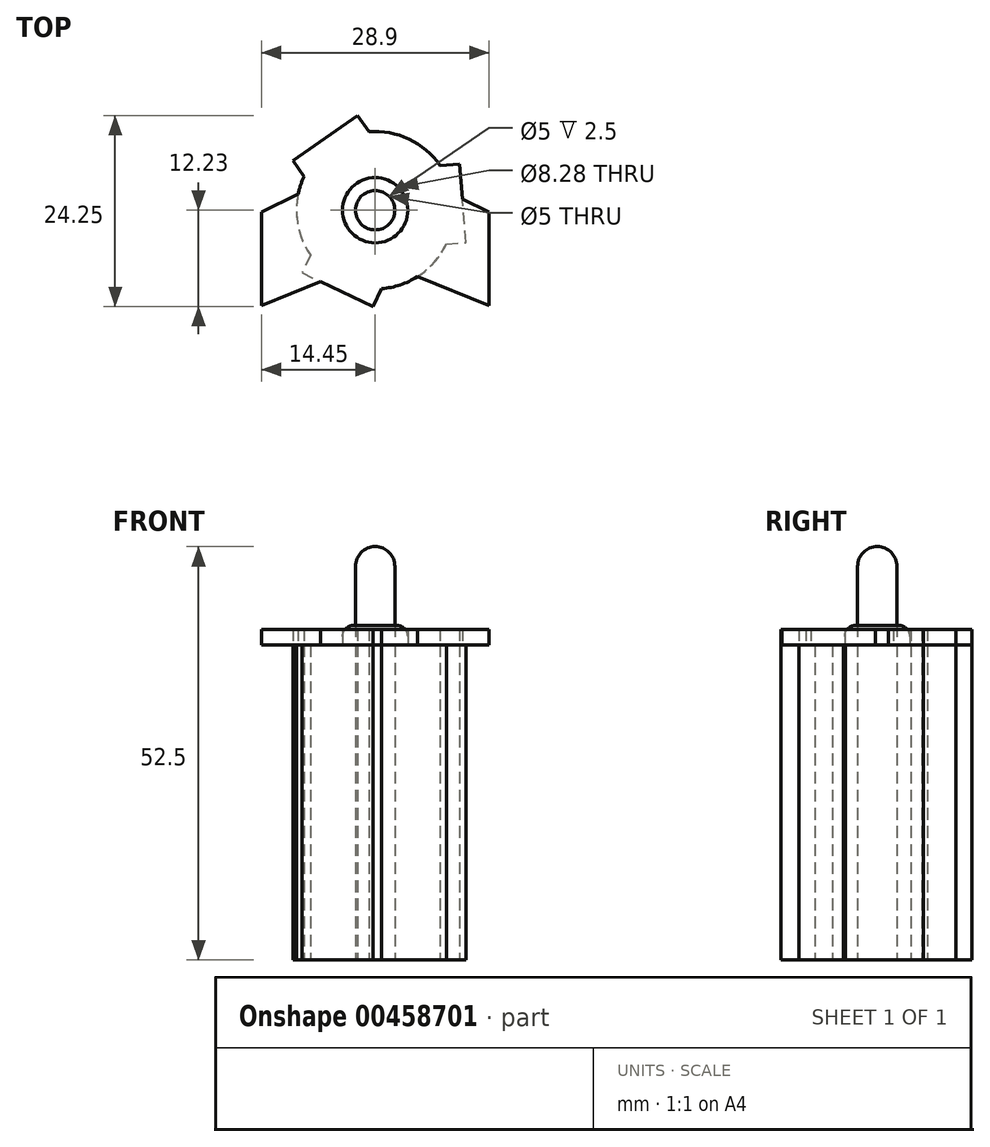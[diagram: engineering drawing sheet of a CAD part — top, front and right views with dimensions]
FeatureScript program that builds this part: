
annotation { "Feature Type Name" : "Feature", "Feature Type Description" : "" }
export const myFeature = defineFeature(function(context is Context, id is Id, definition is map)
    precondition{}
    {
        {
            var Q0;
            Q0=qCreatedBy(makeId("Top.planeOp"),FACE);
            var sketch = newSketch(context, id + "F0", { "sketchPlane" : qUnion([Q0])});
            skCircle(sketch, "E0", {"center": v(0, 0) * mm, "radius": 10 * mm});
            skLineSegment(sketch, "E1", {"start": v(-9.04, 4.28) * mm, "end": v(-0.81, 9.97) * mm});
            skLineSegment(sketch, "E2", {"start": v(-0.81, 9.97) * mm, "end": v(-2.23, 12.02) * mm});
            skLineSegment(sketch, "E3", {"start": v(-2.23, 12.02) * mm, "end": v(-10.46, 6.34) * mm});
            skLineSegment(sketch, "E4", {"start": v(-10.46, 6.34) * mm, "end": v(-9.04, 4.28) * mm});
            skLineSegment(sketch, "E5.1.0", {"start": v(-8.23, -5.69) * mm, "end": v(-9.3, -7.95) * mm});
            skLineSegment(sketch, "E5.1.1", {"start": v(-0.26, -12.23) * mm, "end": v(0.81, -9.97) * mm});
            skLineSegment(sketch, "E5.1.2", {"start": v(-9.3, -7.95) * mm, "end": v(-0.26, -12.23) * mm});
            skLineSegment(sketch, "E5.2.0", {"start": v(9.04, -4.28) * mm, "end": v(11.53, -4.08) * mm});
            skLineSegment(sketch, "E5.2.1", {"start": v(10.72, 5.89) * mm, "end": v(8.23, 5.69) * mm});
            skLineSegment(sketch, "E5.2.2", {"start": v(11.53, -4.08) * mm, "end": v(10.72, 5.89) * mm});
            skCircle(sketch, "E6", {"center": v(0, 0) * mm, "radius": 2.5 * mm});
            skSolve(sketch);
        }
        {
            var Q0;
            Q0 = qSketchRegion(id + "F0", true);
            extrude(context, id + "F1", {"entities" : qUnion([Q0]), "depth" : 40 * mm, "offsetDistance" : 25 * mm});
        }
        {
            var Q0;
            Q0=makeQuery(id+"F0.imprint","IMPRINT",FACE,{"disambiguationData":[TD([[makeQuery(id+"F0.imprint","IMPRINT",EDGE,{"derivedFrom":sQuery(id+"F0.wireOp",EDGE,"E6")}),1.0]])]});
            extrude(context, id + "F2", {"entities" : qUnion([Q0]), "depth" : 40 * mm, "offsetDistance" : 25 * mm});
        }
        {
            var Q0;
            Q0=makeQuery(id+"F1.opExtrude","CAP_FACE",FACE,{"disambiguationData":[OSD([sQuery(id+"F0.wireOp",EDGE,"E0"),sQuery(id+"F0.wireOp",EDGE,"E2"),sQuery(id+"F0.wireOp",EDGE,"E3"),sQuery(id+"F0.wireOp",EDGE,"E4"),sQuery(id+"F0.wireOp",EDGE,"E5.1.0"),sQuery(id+"F0.wireOp",EDGE,"E5.1.1"),sQuery(id+"F0.wireOp",EDGE,"E5.1.2"),sQuery(id+"F0.wireOp",EDGE,"E5.2.0"),sQuery(id+"F0.wireOp",EDGE,"E5.2.1"),sQuery(id+"F0.wireOp",EDGE,"E5.2.2"),sQuery(id+"F0.wireOp",EDGE,"E6")])],"isStart":false});
            var sketch = newSketch(context, id + "F3", { "sketchPlane" : qUnion([Q0])});
            skLineSegment(sketch, "E7", {"start": v(0, 4.61) * mm, "end": v(-14.45, -2.48) * mm});
            skLineSegment(sketch, "E8", {"start": v(0, -4.14) * mm, "end": v(-14.45, -9.95) * mm});
            skCircle(sketch, "E9", {"center": v(0, 0) * mm, "radius": 4.14 * mm});
            skLineSegment(sketch, "E10.1", {"start": v(0, 6.84) * mm, "end": v(-14.45, -0.26) * mm});
            skLineSegment(sketch, "E11.1", {"start": v(-0.08, -6.33) * mm, "end": v(-14.45, -12.1) * mm});
            skLineSegment(sketch, "E12", {"start": v(-14.45, -0.26) * mm, "end": v(-14.45, -12.1) * mm});
            skLineSegment(sketch, "E13.MirrorCS", {"start": v(0, 6.84) * mm, "end": v(14.45, -0.26) * mm});
            skLineSegment(sketch, "E14.MirrorCS", {"start": v(0, 4.61) * mm, "end": v(14.45, -2.48) * mm});
            skLineSegment(sketch, "E15.MirrorCS", {"start": v(0, -4.14) * mm, "end": v(14.45, -9.95) * mm});
            skLineSegment(sketch, "E16.MirrorCS", {"start": v(0.08, -6.33) * mm, "end": v(14.45, -12.1) * mm});
            skLineSegment(sketch, "E17.MirrorCS", {"start": v(14.45, -0.26) * mm, "end": v(14.45, -12.1) * mm});
            skSolve(sketch);
        }
        {
            var Q0;
            Q0=makeQuery(id+"F3.imprint","IMPRINT",FACE,{"disambiguationData":[TD([[makeQuery(id+"F3.imprint","IMPRINT",EDGE,{"derivedFrom":makeQuery(id+"F1.opExtrude","CAP_EDGE",EDGE,{"disambiguationData":[OSD([sQuery(id+"F0.wireOp",EDGE,"E6")])],"isStart":false})}),1.0]])]});
            extrude(context, id + "F4", {"entities" : qUnion([Q0]), "depth" : 10 * mm, "offsetDistance" : 25 * mm});
        }
        {
            var Q0;
            Q0=makeQuery(id+"F3.imprint","IMPRINT",FACE,{"disambiguationData":[TD([[makeQuery(id+"F3.imprint","IMPRINT",EDGE,{"derivedFrom":makeQuery(id+"F1.opExtrude","CAP_EDGE",EDGE,{"disambiguationData":[OSD([sQuery(id+"F0.wireOp",EDGE,"E6")])],"isStart":false})}),-1.0]])]});
            extrude(context, id + "F5", {"entities" : qUnion([Q0]), "depth" : 2.5 * mm, "offsetDistance" : 25 * mm});
        }
        {
            var Q0;
            Q0=qCreatedBy(makeId("Front.planeOp"),FACE);
            var sketch = newSketch(context, id + "F6", { "sketchPlane" : qUnion([Q0])});
            skArc(sketch, "E18", {"start": v(2.5, 50) * mm, "mid": v(0, 52.5) * mm, "end": v(-2.5, 50) * mm});
            skLineSegment(sketch, "E19", {"start": v(2.5, 50) * mm, "end": v(-2.5, 50) * mm});
            skSolve(sketch);
        }
        {
            var Q0;
            Q0=makeQuery(id+"F6.imprint","IMPRINT",FACE,{"disambiguationData":[TD([[makeQuery(id+"F6.imprint","IMPRINT",EDGE,{"derivedFrom":sQuery(id+"F6.wireOp",EDGE,"E18")}),1.0]])]});
            var Q1;
            Q1=sQuery(id+"F6.wireOp",EDGE,"E19");
            revolve(context, id + "F7", {"operationType" : NewBodyOperationType.ADD, "entities" : qUnion([Q0]), "axis" : qUnion([Q1]), "revolveType" : RevolveType.FULL});
        }
        {
            var Q0;
            Q0=makeQuery(id+"F5.opExtrude","CAP_EDGE",EDGE,{"disambiguationData":[OSD([sQuery(id+"F3.wireOp",EDGE,"E9")])],"isStart":false});
            fillet(context, id + "F8", {"entities" : qUnion([Q0]), "radius" : 1.4 * mm, "tangentPropagation" : true, "allowEdgeOverflow" : false});
        }
        {
            var Q0;
            {var subQ0=sQuery(id+"F0.wireOp",EDGE,"E5.2.0");var subQ1=makeQuery(id+"F1.opExtrude","CAP_EDGE",EDGE,{"disambiguationData":[OSD([subQ0])],"isStart":false});Q0=makeQuery(id+"F3.imprint","IMPRINT",FACE,{"disambiguationData":[TD([[makeQuery(id+"F3.imprint","IMPRINT",EDGE,{"derivedFrom":subQ1}),1.0]])]});}
            var Q1;
            {var subQ0=sQuery(id+"F3.wireOp",EDGE,"E14.MirrorCS");var subQ1=sQuery(id+"F3.wireOp",EDGE,"E7");var subQ2=makeQuery(id+"F3.imprint","INTERSECT",VERTEX,{"derivedFrom":[subQ1,subQ0]});Q1=makeQuery(id+"F3.imprint","IMPRINT",FACE,{"disambiguationData":[TD([[makeQuery(id+"F3.imprint","IMPRINT",EDGE,{"disambiguationData":[TD([[subQ2,-1.0]])],"derivedFrom":subQ1}),1.0]])]});}
            var Q2;
            {var subQ7=sQuery(id+"F3.wireOp",EDGE,"E12");var subQ9=sQuery(id+"F3.wireOp",EDGE,"E8");var subQ10=makeQuery(id+"F3.imprint","INTERSECT",VERTEX,{"derivedFrom":[subQ9,subQ7]});Q2=makeQuery(id+"F3.imprint","IMPRINT",FACE,{"disambiguationData":[TD([[makeQuery(id+"F3.imprint","IMPRINT",EDGE,{"disambiguationData":[TD([[subQ10,1.0]])],"derivedFrom":subQ9}),-1.0]])]});}
            var Q3;
            {var subQ0=sQuery(id+"F0.wireOp",EDGE,"E5.1.0");var subQ1=makeQuery(id+"F1.opExtrude","CAP_EDGE",EDGE,{"disambiguationData":[OSD([subQ0])],"isStart":false});var subQ9=sQuery(id+"F3.wireOp",EDGE,"E8");var subQ11=makeQuery(id+"F3.imprint","INTERSECT",VERTEX,{"derivedFrom":[subQ1,subQ9]});Q3=makeQuery(id+"F3.imprint","IMPRINT",FACE,{"disambiguationData":[TD([[makeQuery(id+"F3.imprint","IMPRINT",EDGE,{"disambiguationData":[TD([[subQ11,1.0]])],"derivedFrom":subQ9}),-1.0]])]});}
            var Q4;
            {var subQ0=sQuery(id+"F0.wireOp",EDGE,"E5.2.0");var subQ1=makeQuery(id+"F1.opExtrude","CAP_EDGE",EDGE,{"disambiguationData":[OSD([subQ0])],"isStart":false});Q4=makeQuery(id+"F3.imprint","IMPRINT",FACE,{"disambiguationData":[TD([[makeQuery(id+"F3.imprint","IMPRINT",EDGE,{"derivedFrom":subQ1}),-1.0]])]});}
            var Q5;
            {var subQ0=sQuery(id+"F3.wireOp",EDGE,"E12");var subQ1=sQuery(id+"F3.wireOp",EDGE,"E7");var subQ2=makeQuery(id+"F3.imprint","INTERSECT",VERTEX,{"derivedFrom":[subQ1,subQ0]});Q5=makeQuery(id+"F3.imprint","IMPRINT",FACE,{"disambiguationData":[TD([[makeQuery(id+"F3.imprint","IMPRINT",EDGE,{"disambiguationData":[TD([[subQ2,1.0]])],"derivedFrom":subQ0}),1.0]])]});}
            var Q6;
            {var subQ0=sQuery(id+"F3.wireOp",EDGE,"E17.MirrorCS");var subQ1=sQuery(id+"F3.wireOp",EDGE,"E13.MirrorCS");var subQ2=makeQuery(id+"F3.imprint","INTERSECT",VERTEX,{"derivedFrom":[subQ1,subQ0]});Q6=makeQuery(id+"F3.imprint","IMPRINT",FACE,{"disambiguationData":[TD([[makeQuery(id+"F3.imprint","IMPRINT",EDGE,{"disambiguationData":[TD([[subQ2,1.0]])],"derivedFrom":subQ1}),-1.0]])]});}
            var Q7;
            {var subQ0=sQuery(id+"F3.wireOp",EDGE,"E17.MirrorCS");var subQ1=sQuery(id+"F3.wireOp",EDGE,"E15.MirrorCS");var subQ2=makeQuery(id+"F3.imprint","INTERSECT",VERTEX,{"derivedFrom":[subQ1,subQ0]});Q7=makeQuery(id+"F3.imprint","IMPRINT",FACE,{"disambiguationData":[TD([[makeQuery(id+"F3.imprint","IMPRINT",EDGE,{"disambiguationData":[TD([[subQ2,-1.0]])],"derivedFrom":subQ0}),-1.0]])]});}
            var Q8;
            {var subQ0=sQuery(id+"F3.wireOp",EDGE,"E12");var subQ1=sQuery(id+"F3.wireOp",EDGE,"E8");var subQ2=makeQuery(id+"F3.imprint","INTERSECT",VERTEX,{"derivedFrom":[subQ1,subQ0]});Q8=makeQuery(id+"F3.imprint","IMPRINT",FACE,{"disambiguationData":[TD([[makeQuery(id+"F3.imprint","IMPRINT",EDGE,{"disambiguationData":[TD([[subQ2,1.0]])],"derivedFrom":subQ1}),1.0]])]});}
            var Q9;
            {var subQ9=sQuery(id+"F3.wireOp",EDGE,"E7");var subQ12=sQuery(id+"F3.wireOp",EDGE,"E14.MirrorCS");var subQ14=makeQuery(id+"F3.imprint","INTERSECT",VERTEX,{"derivedFrom":[subQ9,subQ12]});Q9=makeQuery(id+"F3.imprint","IMPRINT",FACE,{"disambiguationData":[TD([[makeQuery(id+"F3.imprint","IMPRINT",EDGE,{"disambiguationData":[TD([[subQ14,-1.0]])],"derivedFrom":subQ9}),-1.0]])]});}
            var Q10;
            {var subQ0=sQuery(id+"F0.wireOp",EDGE,"E5.1.1");var subQ1=makeQuery(id+"F1.opExtrude","CAP_EDGE",EDGE,{"disambiguationData":[OSD([subQ0])],"isStart":false});Q10=makeQuery(id+"F3.imprint","IMPRINT",FACE,{"disambiguationData":[TD([[makeQuery(id+"F3.imprint","IMPRINT",EDGE,{"derivedFrom":subQ1}),1.0]])]});}
            var Q11;
            {var subQ0=sQuery(id+"F0.wireOp",EDGE,"E2");Q11=makeQuery(id+"F3.imprint","IMPRINT",FACE,{"disambiguationData":[TD([[makeQuery(id+"F3.imprint","IMPRINT",EDGE,{"derivedFrom":makeQuery(id+"F1.opExtrude","CAP_EDGE",EDGE,{"disambiguationData":[OSD([subQ0])],"isStart":false})}),1.0]])]});}
            extrude(context, id + "F9", {"entities" : qUnion([Q0, Q1, Q2, Q3, Q4, Q5, Q6, Q7, Q8, Q9, Q10, Q11]), "depth" : 2 * mm, "offsetDistance" : 25 * mm});
        }
    });
